# Revit family: Legrand XL³-S 160 saliente
name_source: partatom
category: Equipement électrique
units: mm (PartAtom-declared; Revit-internal decimal feet)

## family parameters
Basée sur le plan de construction = Non
Configuration du panneau = Deux colonnes, circuits au sein
Cote de connecteur circulaire = Utiliser le diamètre
Couper avec des vides une fois chargée = Non
Numéro OmniClass = 23.80.30.11.17
Partagée = Non
Point de calcul de pièce = Non
Titre OmniClass = Distribution Boards and Control Panels
Toujours verticalement = Oui
Type d'élément = Tableau de raccordement

## types (12) — shared parameters
Condiciones Generales de Uso = https://export.legrand.com
ETIM Class 6.0 = EC000261
Fabricant = Legrand
IK = 07
IP = 40
Image du type = XL3S160_saillie_337204_p_230125.jpg
Materia = Acero
RAL = 9003
URL = www.legrand.fr
distancia lado asentamiento = 135 mm  [stored 0.442913 ft]
profundidad = 135 mm  [stored 0.442913 ft]
puerta = Oui
zero-valued in all types: Elévation par défaut

## per-type parameters (varying)
- Envolvente de distribución - XL³ S 160 -  Metal - caja saliente - 24 módulos - 2 filas: Altura=440 mm  [stored 1.44357 ft]; Caja 337202=Oui; Caja 337203=Non; Caja 337204=Non; Caja 337205=Non; Caja 337206=Non; Caja 337207=Non; Caja 337208=Non; Caja 337214=Non; Caja 337215=Non; Caja 337216=Non; Caja 337217=Non; Caja 337218=Non; Description=337202  Envolvente de distribución - XL³ S 160 -  Metal - caja saliente - 24 módulos - 2 filas; anchura=595 mm  [stored 1.9521 ft]; anchura asentamiento=865 mm  [stored 2.83793 ft]; distancia antes de asentamiento=595 mm  [stored 1.9521 ft]; profundidad asentamiento=730 mm  [stored 2.39501 ft]; puerta 337252=Oui; puerta 337253=Non; puerta 337254=Non; puerta 337255=Non; puerta 337256=Non; puerta 337257=Non; puerta 337258=Non; puerta 337264=Non; puerta 337265=Non; puerta 337266=Non; puerta 337267=Non; puerta 337268=Non
- Envolvente de distribución - XL³ S 160 -  Metal - caja saliente - 24 módulos - 3 filas: Altura=590 mm  [stored 1.9357 ft]; Caja 337202=Non; Caja 337203=Oui; Caja 337204=Non; Caja 337205=Non; Caja 337206=Non; Caja 337207=Non; Caja 337208=Non; Caja 337214=Non; Caja 337215=Non; Caja 337216=Non; Caja 337217=Non; Caja 337218=Non; Description=337203  Envolvente de distribución - XL³ S 160 -  Metal - caja saliente - 24 módulos - 3 filas; anchura=595 mm  [stored 1.9521 ft]; anchura asentamiento=865 mm  [stored 2.83793 ft]; distancia antes de asentamiento=595 mm  [stored 1.9521 ft]; profundidad asentamiento=730 mm  [stored 2.39501 ft]; puerta 337252=Non; puerta 337253=Oui; puerta 337254=Non; puerta 337255=Non; puerta 337256=Non; puerta 337257=Non; puerta 337258=Non; puerta 337264=Non; puerta 337265=Non; puerta 337266=Non; puerta 337267=Non; puerta 337268=Non
- Envolvente de distribución - XL³ S 160 -  Metal - caja saliente - 24 módulos - 4 filas: Altura=740 mm  [stored 2.42782 ft]; Caja 337202=Non; Caja 337203=Non; Caja 337204=Oui; Caja 337205=Non; Caja 337206=Non; Caja 337207=Non; Caja 337208=Non; Caja 337214=Non; Caja 337215=Non; Caja 337216=Non; Caja 337217=Non; Caja 337218=Non; Description=337204  Envolvente de distribución - XL³ S 160 -  Metal - caja saliente - 24 módulos - 4 filas; anchura=595 mm  [stored 1.9521 ft]; anchura asentamiento=865 mm  [stored 2.83793 ft]; distancia antes de asentamiento=595 mm  [stored 1.9521 ft]; profundidad asentamiento=730 mm  [stored 2.39501 ft]; puerta 337252=Non; puerta 337253=Non; puerta 337254=Oui; puerta 337255=Non; puerta 337256=Non; puerta 337257=Non; puerta 337258=Non; puerta 337264=Non; puerta 337265=Non; puerta 337266=Non; puerta 337267=Non; puerta 337268=Non
- Envolvente de distribución - XL³ S 160 -  Metal - caja saliente - 24 módulos - 5 filas: Altura=890 mm  [stored 2.91995 ft]; Caja 337202=Non; Caja 337203=Non; Caja 337204=Non; Caja 337205=Oui; Caja 337206=Non; Caja 337207=Non; Caja 337208=Non; Caja 337214=Non; Caja 337215=Non; Caja 337216=Non; Caja 337217=Non; Caja 337218=Non; Description=337205  Envolvente de distribución - XL³ S 160 -  Metal - caja saliente - 24 módulos - 6 filas; anchura=595 mm  [stored 1.9521 ft]; anchura asentamiento=865 mm  [stored 2.83793 ft]; distancia antes de asentamiento=595 mm  [stored 1.9521 ft]; profundidad asentamiento=730 mm  [stored 2.39501 ft]; puerta 337252=Non; puerta 337253=Non; puerta 337254=Non; puerta 337255=Oui; puerta 337256=Non; puerta 337257=Non; puerta 337258=Non; puerta 337264=Non; puerta 337265=Non; puerta 337266=Non; puerta 337267=Non; puerta 337268=Non
- Envolvente de distribución - XL³ S 160 -  Metal - caja saliente - 24 módulos - 6 filas: Altura=1040 mm  [stored 3.41207 ft]; Caja 337202=Non; Caja 337203=Non; Caja 337204=Non; Caja 337205=Non; Caja 337206=Oui; Caja 337207=Non; Caja 337208=Non; Caja 337214=Non; Caja 337215=Non; Caja 337216=Non; Caja 337217=Non; Caja 337218=Non; Description=337206  Envolvente de distribución - XL³ S 160 -  Metal - caja saliente - 24 módulos - 7 filas; anchura=595 mm  [stored 1.9521 ft]; anchura asentamiento=865 mm  [stored 2.83793 ft]; distancia antes de asentamiento=595 mm  [stored 1.9521 ft]; profundidad asentamiento=730 mm  [stored 2.39501 ft]; puerta 337252=Non; puerta 337253=Non; puerta 337254=Non; puerta 337255=Non; puerta 337256=Oui; puerta 337257=Non; puerta 337258=Non; puerta 337264=Non; puerta 337265=Non; puerta 337266=Non; puerta 337267=Non; puerta 337268=Non
- Envolvente de distribución - XL³ S 160 -  Metal - caja saliente - 24 módulos - 7 filas: Altura=1190 mm  [stored 3.9042 ft]; Caja 337202=Non; Caja 337203=Non; Caja 337204=Non; Caja 337205=Non; Caja 337206=Non; Caja 337207=Oui; Caja 337208=Non; Caja 337214=Non; Caja 337215=Non; Caja 337216=Non; Caja 337217=Non; Caja 337218=Non; Description=337207  Envolvente de distribución - XL³ S 160 -  Metal - caja saliente - 24 módulos - 7 filas; anchura=595 mm  [stored 1.9521 ft]; anchura asentamiento=865 mm  [stored 2.83793 ft]; distancia antes de asentamiento=595 mm  [stored 1.9521 ft]; profundidad asentamiento=730 mm  [stored 2.39501 ft]; puerta 337252=Non; puerta 337253=Non; puerta 337254=Non; puerta 337255=Non; puerta 337256=Non; puerta 337257=Oui; puerta 337258=Non; puerta 337264=Non; puerta 337265=Non; puerta 337266=Non; puerta 337267=Non; puerta 337268=Non
- Envolvente de distribución - XL³ S 160 -  Metal - caja saliente - 24 módulos - 8 filas: Altura=1340 mm  [stored 4.39633 ft]; Caja 337202=Non; Caja 337203=Non; Caja 337204=Non; Caja 337205=Non; Caja 337206=Non; Caja 337207=Non; Caja 337208=Oui; Caja 337214=Non; Caja 337215=Non; Caja 337216=Non; Caja 337217=Non; Caja 337218=Non; Description=337208  Envolvente de distribución - XL³ S 160 -  Metal - caja saliente - 24 módulos - 8 filas; anchura=595 mm  [stored 1.9521 ft]; anchura asentamiento=865 mm  [stored 2.83793 ft]; distancia antes de asentamiento=595 mm  [stored 1.9521 ft]; profundidad asentamiento=730 mm  [stored 2.39501 ft]; puerta 337252=Non; puerta 337253=Non; puerta 337254=Non; puerta 337255=Non; puerta 337256=Non; puerta 337257=Non; puerta 337258=Oui; puerta 337264=Non; puerta 337265=Non; puerta 337266=Non; puerta 337267=Non; puerta 337268=Non
- Envolvente de distribución - XL³ S 160 -  Metal - caja saliente - 36 módulos - 4 filas: Altura=740 mm  [stored 2.42782 ft]; Caja 337202=Non; Caja 337203=Non; Caja 337204=Non; Caja 337205=Non; Caja 337206=Non; Caja 337207=Non; Caja 337208=Non; Caja 337214=Oui; Caja 337215=Non; Caja 337216=Non; Caja 337217=Non; Caja 337218=Non; Description=337214  Envolvente de distribución - XL³ S 160 -  Metal - caja saliente - 36 módulos - 4 filas; anchura=810 mm; anchura asentamiento=1080 mm  [stored 3.54331 ft]; distancia antes de asentamiento=810 mm; profundidad asentamiento=945 mm; puerta 337252=Non; puerta 337253=Non; puerta 337254=Non; puerta 337255=Non; puerta 337256=Non; puerta 337257=Non; puerta 337258=Non; puerta 337264=Oui; puerta 337265=Non; puerta 337266=Non; puerta 337267=Non; puerta 337268=Non
- Envolvente de distribución - XL³ S 160 -  Metal - caja saliente - 36 módulos - 5 filas: Altura=890 mm  [stored 2.91995 ft]; Caja 337202=Non; Caja 337203=Non; Caja 337204=Non; Caja 337205=Non; Caja 337206=Non; Caja 337207=Non; Caja 337208=Non; Caja 337214=Non; Caja 337215=Oui; Caja 337216=Non; Caja 337217=Non; Caja 337218=Non; Description=337215  Envolvente de distribución - XL³ S 160 -  Metal - caja saliente - 36 módulos - 5 filas; anchura=810 mm; anchura asentamiento=1080 mm  [stored 3.54331 ft]; distancia antes de asentamiento=810 mm; profundidad asentamiento=945 mm; puerta 337252=Non; puerta 337253=Non; puerta 337254=Non; puerta 337255=Non; puerta 337256=Non; puerta 337257=Non; puerta 337258=Non; puerta 337264=Non; puerta 337265=Oui; puerta 337266=Non; puerta 337267=Non; puerta 337268=Non
- Envolvente de distribución - XL³ S 160 -  Metal - caja saliente - 36 módulos - 6 filas: Altura=1040 mm  [stored 3.41207 ft]; Caja 337202=Non; Caja 337203=Non; Caja 337204=Non; Caja 337205=Non; Caja 337206=Non; Caja 337207=Non; Caja 337208=Non; Caja 337214=Non; Caja 337215=Non; Caja 337216=Oui; Caja 337217=Non; Caja 337218=Non; Description=337216  Envolvente de distribución - XL³ S 160 -  Metal - caja saliente - 36 módulos - 6 filas; anchura=810 mm; anchura asentamiento=1080 mm  [stored 3.54331 ft]; distancia antes de asentamiento=810 mm; profundidad asentamiento=945 mm; puerta 337252=Non; puerta 337253=Non; puerta 337254=Non; puerta 337255=Non; puerta 337256=Non; puerta 337257=Non; puerta 337258=Non; puerta 337264=Non; puerta 337265=Non; puerta 337266=Oui; puerta 337267=Non; puerta 337268=Non
- Envolvente de distribución - XL³ S 160 -  Metal - caja saliente - 36 módulos - 7 filas: Altura=1190 mm  [stored 3.9042 ft]; Caja 337202=Non; Caja 337203=Non; Caja 337204=Non; Caja 337205=Non; Caja 337206=Non; Caja 337207=Non; Caja 337208=Non; Caja 337214=Non; Caja 337215=Non; Caja 337216=Non; Caja 337217=Oui; Caja 337218=Non; Description=337217  Envolvente de distribución - XL³ S 160 -  Metal - caja saliente - 36 módulos - 7 filas; anchura=810 mm; anchura asentamiento=1080 mm  [stored 3.54331 ft]; distancia antes de asentamiento=810 mm; profundidad asentamiento=945 mm; puerta 337252=Non; puerta 337253=Non; puerta 337254=Non; puerta 337255=Non; puerta 337256=Non; puerta 337257=Non; puerta 337258=Non; puerta 337264=Non; puerta 337265=Non; puerta 337266=Non; puerta 337267=Oui; puerta 337268=Non
- Envolvente de distribución - XL³ S 160 -  Metal - caja saliente - 36 módulos - 8 filas: Altura=1340 mm  [stored 4.39633 ft]; Caja 337202=Non; Caja 337203=Non; Caja 337204=Non; Caja 337205=Non; Caja 337206=Non; Caja 337207=Non; Caja 337208=Non; Caja 337214=Non; Caja 337215=Non; Caja 337216=Non; Caja 337217=Non; Caja 337218=Oui; Description=337218  Envolvente de distribución - XL³ S 160 -  Metal - caja saliente - 36 módulos - 8 filas; anchura=810 mm; anchura asentamiento=1080 mm  [stored 3.54331 ft]; distancia antes de asentamiento=810 mm; profundidad asentamiento=945 mm; puerta 337252=Non; puerta 337253=Non; puerta 337254=Non; puerta 337255=Non; puerta 337256=Non; puerta 337257=Non; puerta 337258=Non; puerta 337264=Non; puerta 337265=Non; puerta 337266=Non; puerta 337267=Non; puerta 337268=Oui

note: [stored X ft] marks values corroborated as IEEE doubles in the binary element streams (Revit-internal decimal feet)
